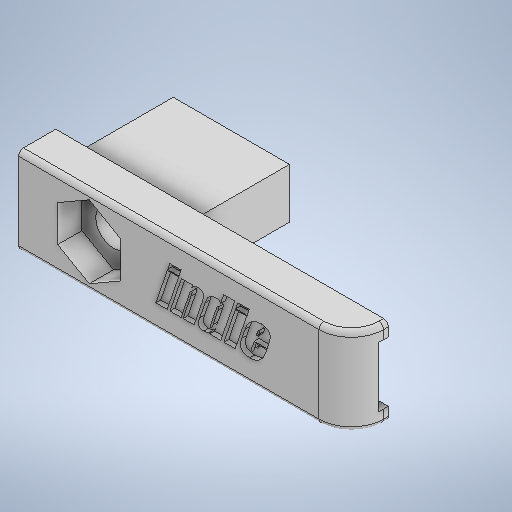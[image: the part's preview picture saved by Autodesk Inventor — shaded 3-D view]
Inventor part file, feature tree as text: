
AUTODESK INVENTOR PART (.ipt)
format: ipt  version: 2025 (Build 290162000, 162)  size: 427,008 bytes
history: native  units: mm
features: reference x14, extrude x5, other x4, fillet x2, sketch x2, emboss x1, projected_geometry x1
ambient origin geometry x8: Origin, YZ Plane, XZ Plane, XY Plane, X Axis, Y Axis, Z Axis, Center Point
bodies: Solid1 (feature_tree)
feature tree (29):
  extrude  "Extrusion1"  Depth=1.7mm TaperAngle=0.0deg
  extrude  "Extrusion2"  Depth=2.0mm
  fillet  "Fillet1"  Radius=0.15mm
  extrude  "Extrusion5"  Depth=0.3mm
  extrude  "Extrusion7"  Depth=0.3mm
  extrude  "Extrusion8"  Depth=0.3mm
  fillet  "Fillet2"  Radius=6.5mm
  emboss  "Emboss1"
  reference  "Reference1"
  reference  "Reference2"
  reference  "Reference3"
  reference  "Reference13"
  reference  "Reference14"
  reference  "Reference15"
  reference  "Reference16"
  reference  "Reference17"
  sketch  "Sketch6"  dims[d1=20.6mm d2=1.7mm d3=0.0mm]
  reference  "Reference29"
  reference  "Reference31"
  reference  "Reference32"
  projected_geometry  "Projected Loop2"
  reference  "Reference33"
  reference  "Reference34"
  reference  "Reference35"
  sketch  "Sketch9"  dims[d5=0.6mm d6=0.0mm d13=2.0mm d14=0.15mm d15=0.15mm d16=0.15mm d17=0.15mm d20=6.5mm d21=0.0mm d25=1.5mm d26=0.0mm d27=3.9mm d28=1.5mm d29=0.0mm d32=0.3mm d36=0.0mm d37=0.3mm d38=0.0mm]
  parser-record x1  (decoder bookkeeping rows leaked as tree rows — omitted from the tree; the rows remain in map.json)
  other  "np2_full_assembly.iam"
  other  "np2_stereotax_holder_part1:1"
  other  "np2_main_chassis:1"
note: 1 file-system path scrubbed to <path> (originals preserved in map.json)
